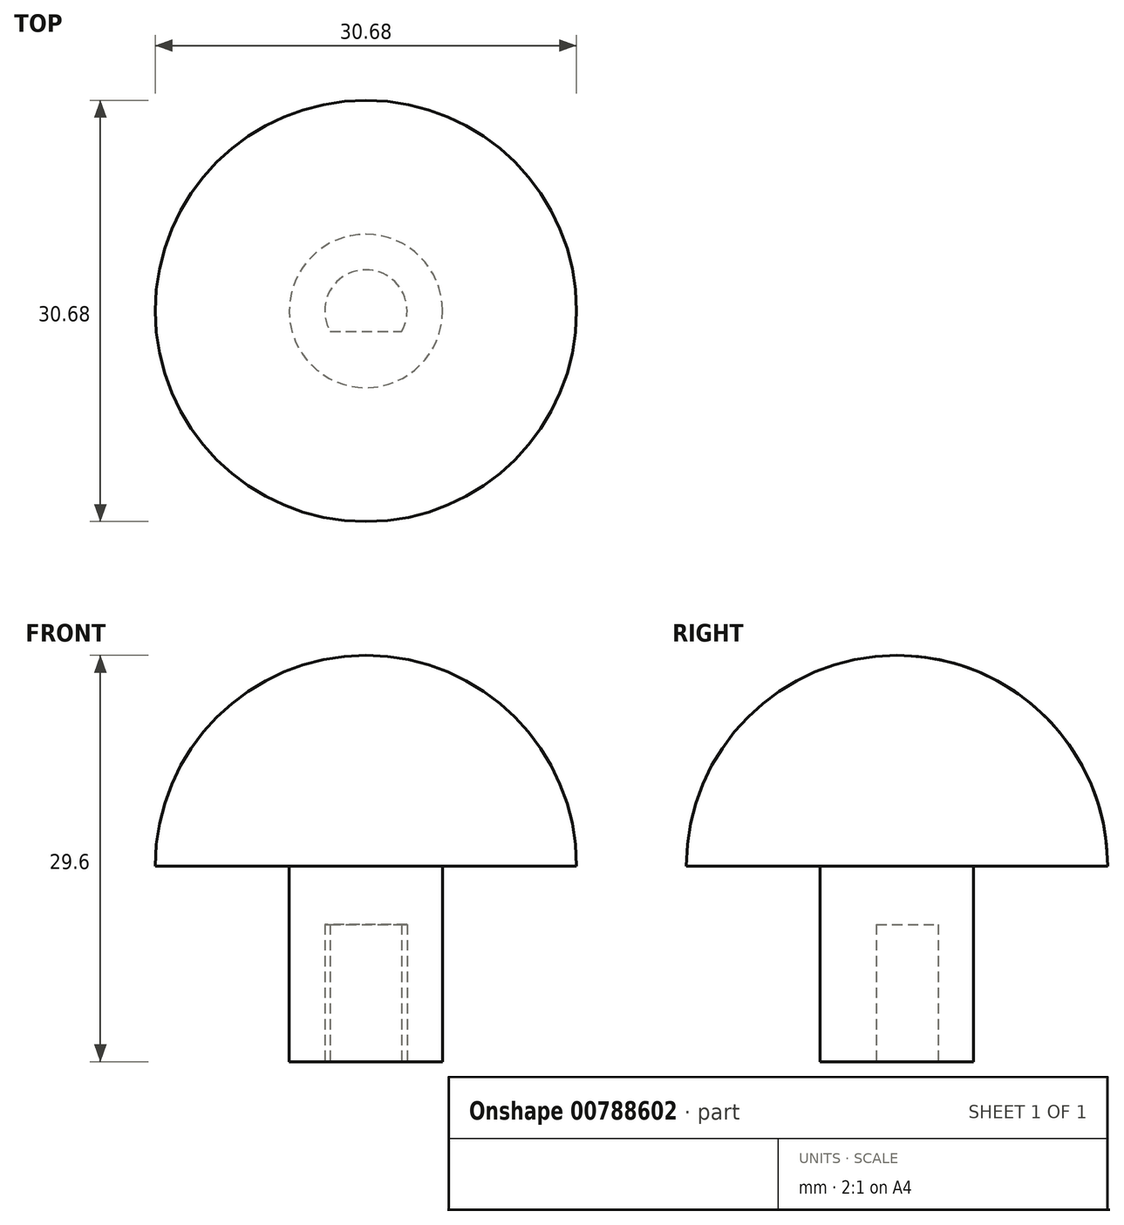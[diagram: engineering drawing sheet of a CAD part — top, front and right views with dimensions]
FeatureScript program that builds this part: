
annotation { "Feature Type Name" : "Feature", "Feature Type Description" : "" }
export const myFeature = defineFeature(function(context is Context, id is Id, definition is map)
    precondition{}
    {
        {
            var Q0;
            Q0=qCreatedBy(makeId("Right.planeOp"),FACE);
            var sketch = newSketch(context, id + "F0", { "sketchPlane" : qUnion([Q0])});
            skLineSegment(sketch, "E0", {"start": v(5.58, 0) * mm, "end": v(5.58, 14.25) * mm});
            skLineSegment(sketch, "E1", {"start": v(5.58, 14.25) * mm, "end": v(15.34, 14.25) * mm});
            skArc(sketch, "E2", {"start": v(15.34, 14.25) * mm, "mid": v(10.85, 25.1) * mm, "end": v(0, 29.6) * mm});
            skLineSegment(sketch, "E3", {"start": v(0, 0) * mm, "end": v(5.58, 0) * mm});
            skLineSegment(sketch, "E4", {"start": v(0, 29.6) * mm, "end": v(0, 0) * mm});
            skSolve(sketch);
        }
        {
            var Q0;
            Q0=makeQuery(id+"F0.imprint","IMPRINT",FACE,{"disambiguationData":[TD([[makeQuery(id+"F0.imprint","IMPRINT",EDGE,{"derivedFrom":sQuery(id+"F0.wireOp",EDGE,"E0")}),1.0]])]});
            var Q1;
            Q1=sQuery(id+"F0.wireOp",EDGE,"E4");
            revolve(context, id + "F1", {"surfaceOperationType" : NewSurfaceOperationType.NEW, "entities" : qUnion([Q0]), "axis" : qUnion([Q1]), "revolveType" : RevolveType.FULL});
        }
        {
            var Q0;
            Q0=qCreatedBy(makeId("Top.planeOp"),FACE);
            var sketch = newSketch(context, id + "F2", { "sketchPlane" : qUnion([Q0])});
            skArc(sketch, "E5", {"start": v(2.6, -1.5) * mm, "mid": v(0, 3) * mm, "end": v(-2.6, -1.5) * mm});
            skLineSegment(sketch, "E6", {"start": v(-2.6, -1.5) * mm, "end": v(2.6, -1.5) * mm});
            skLineSegment(sketch, "E7", {"start": v(0, 3) * mm, "end": v(0, -1.5) * mm, "construction": true});
            skSolve(sketch);
        }
        {
            var Q0;
            Q0=makeQuery(id+"F2.imprint","IMPRINT",FACE,{"disambiguationData":[TD([[makeQuery(id+"F2.imprint","IMPRINT",EDGE,{"derivedFrom":sQuery(id+"F2.wireOp",EDGE,"E5")}),1.0]])]});
            extrude(context, id + "F3", {"entities" : qUnion([Q0]), "operationType" : NewBodyOperationType.REMOVE, "depth" : 10 * mm, "offsetDistance" : 25 * mm});
        }
    });
